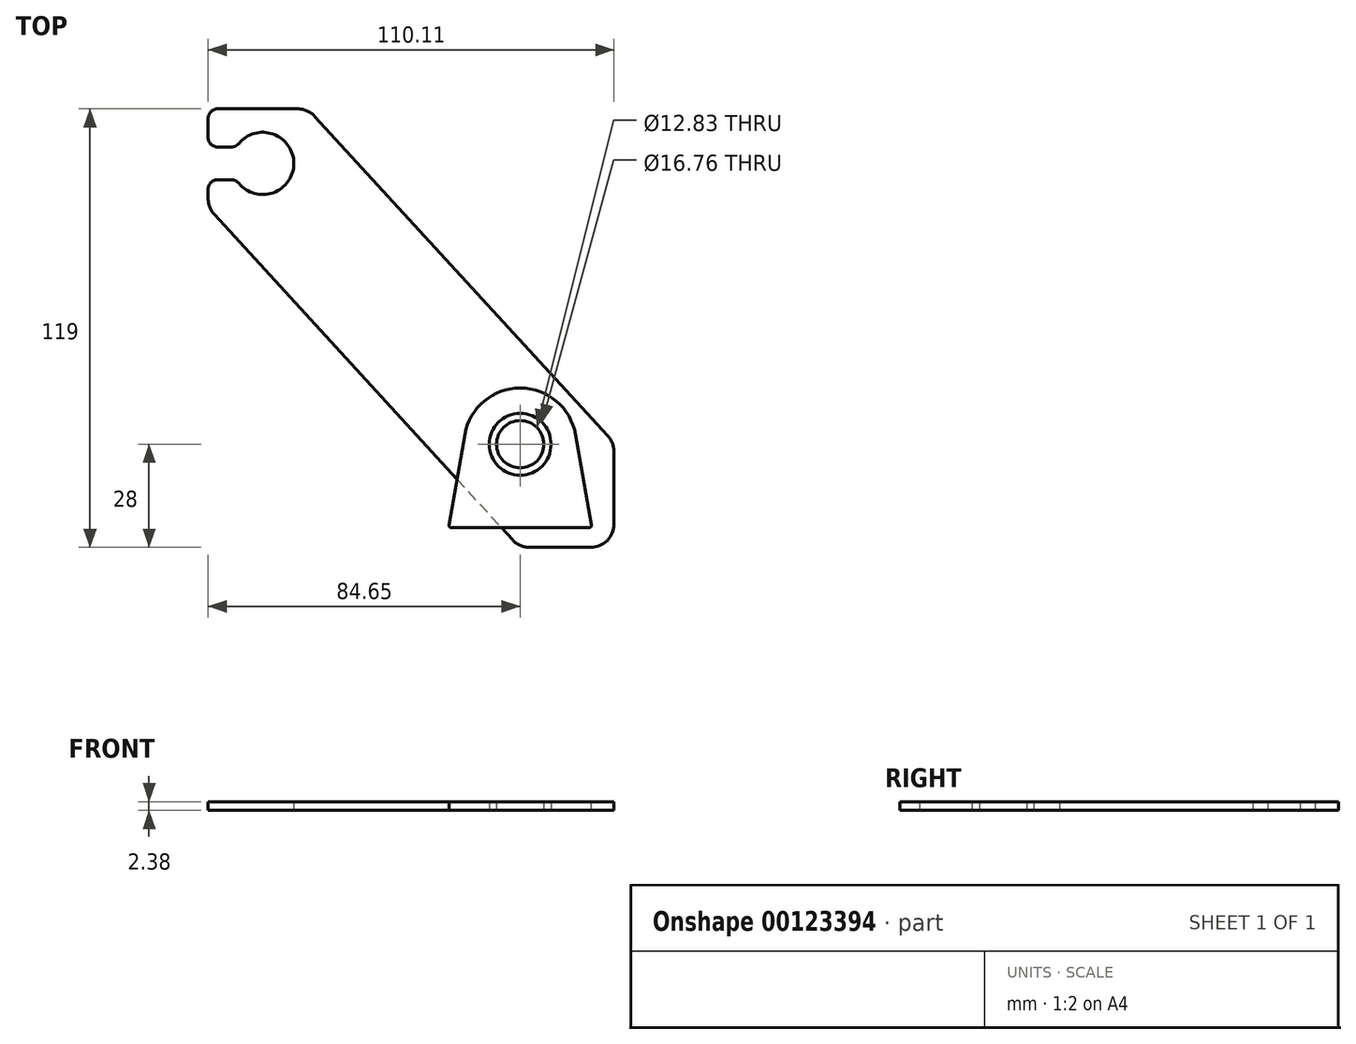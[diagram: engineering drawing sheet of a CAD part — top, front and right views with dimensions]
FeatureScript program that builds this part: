
annotation { "Feature Type Name" : "Feature", "Feature Type Description" : "" }
export const myFeature = defineFeature(function(context is Context, id is Id, definition is map)
    precondition{}
    {
        {
            var Q0;
            Q0=qCreatedBy(makeId("Top.planeOp"),FACE);
            var sketch = newSketch(context, id + "F0", { "sketchPlane" : qUnion([Q0])});
            skCircle(sketch, "E0", {"center": v(0, 0) * mm, "radius": 8.38 * mm});
            skCircle(sketch, "E1", {"center": v(0, 0) * mm, "radius": 8.26 * mm, "construction": true});
            skArc(sketch, "E2", {"start": v(-9.4, -7.26) * mm, "mid": v(0, -11.87) * mm, "end": v(9.4, -7.26) * mm, "construction": true});
            skLineSegment(sketch, "E3", {"start": v(-9.4, 7.26) * mm, "end": v(-9.4, -7.26) * mm, "construction": true});
            skLineSegment(sketch, "E4", {"start": v(0, 17.47) * mm, "end": v(0, -14.03) * mm, "construction": true});
            skLineSegment(sketch, "E5.MirrorCS", {"start": v(9.4, 7.26) * mm, "end": v(9.4, -7.26) * mm, "construction": true});
            skArc(sketch, "E6.trimOffspring", {"start": v(9.4, 7.26) * mm, "mid": v(0, 11.87) * mm, "end": v(-9.4, 7.26) * mm, "construction": true});
            skArc(sketch, "E7", {"start": v(15.24, 0) * mm, "mid": v(0, 15.24) * mm, "end": v(-15.24, 0) * mm});
            skArc(sketch, "E8", {"start": v(19.46, -22.61) * mm, "mid": v(0, -17.78) * mm, "end": v(-19.46, -22.61) * mm});
            skCircle(sketch, "E9", {"center": v(0, 0) * mm, "radius": 15.24 * mm});
            skLineSegment(sketch, "E10", {"start": v(-15, 2.65) * mm, "end": v(-19.46, -22.61) * mm});
            skLineSegment(sketch, "E11", {"start": v(-39.12, -20.64) * mm, "end": v(41.91, -20.64) * mm, "construction": true});
            skLineSegment(sketch, "E12.MirrorCS", {"start": v(15, 2.65) * mm, "end": v(19.46, -22.61) * mm});
            skLineSegment(sketch, "E13", {"start": v(-19.46, -22.61) * mm, "end": v(19.46, -22.61) * mm});
            skSolve(sketch);
        }
        {
            var Q0;
            Q0 = qSketchRegion(id + "F0", true);
            extrude(context, id + "F1", {"entities" : qUnion([Q0]), "depth" : 2.38 * mm});
        }
        {
            var Q0;
            Q0=makeQuery(id+"F1.opExtrude","SWEPT_EDGE",EDGE,{"disambiguationData":[OSD([sQuery(id+"F0.wireOp",EDGE,"E8"),sQuery(id+"F0.wireOp",EDGE,"E10")])]});
            var Q1;
            Q1=makeQuery(id+"F1.opExtrude","SWEPT_EDGE",EDGE,{"disambiguationData":[OSD([sQuery(id+"F0.wireOp",EDGE,"E8"),sQuery(id+"F0.wireOp",EDGE,"E12.MirrorCS")])]});
            fillet(context, id + "F2", {"entities" : qUnion([Q0, Q1]), "radius" : 0.64 * mm, "tangentPropagation" : true, "allowEdgeOverflow" : false});
        }
        {
            var Q0;
            Q0=qCreatedBy(makeId("Top.planeOp"),FACE);
            var sketch = newSketch(context, id + "F3", { "sketchPlane" : qUnion([Q0])});
            skCircle(sketch, "E14", {"center": v(0, 0) * mm, "radius": 6.41 * mm});
            skArc(sketch, "E15", {"start": v(-77.03, 71.75) * mm, "mid": v(-61.4, 76.2) * mm, "end": v(-77.03, 80.64) * mm});
            skLineSegment(sketch, "E16.bottom", {"start": v(-84.65, 91) * mm, "end": v(-57.57, 91) * mm});
            skLineSegment(sketch, "E16.top", {"start": v(-0.17, -28) * mm, "end": v(25.46, -28) * mm});
            skLineSegment(sketch, "E16.left", {"start": v(-84.65, 91) * mm, "end": v(-84.65, 80.64) * mm});
            skLineSegment(sketch, "E16.right", {"start": v(25.46, 0.41) * mm, "end": v(25.46, -28) * mm});
            skCircle(sketch, "E17", {"center": v(-69.85, 76.2) * mm, "radius": 14.8 * mm, "construction": true});
            skLineSegment(sketch, "E18", {"start": v(-6.41, 0) * mm, "end": v(-6.41, -28) * mm, "construction": true});
            skLineSegment(sketch, "E19", {"start": v(-84.65, 64.15) * mm, "end": v(-0.17, -28) * mm});
            skLineSegment(sketch, "E20", {"start": v(-57.57, 91) * mm, "end": v(25.46, 0.41) * mm});
            skLineSegment(sketch, "E21", {"start": v(0, 6.41) * mm, "end": v(25.46, 6.41) * mm, "construction": true});
            skLineSegment(sketch, "E22", {"start": v(-69.85, 76.2) * mm, "end": v(-84.65, 76.2) * mm, "construction": true});
            skLineSegment(sketch, "E23", {"start": v(-84.65, 80.64) * mm, "end": v(-77.03, 80.64) * mm});
            skLineSegment(sketch, "E24.MirrorCS", {"start": v(-84.65, 71.75) * mm, "end": v(-77.03, 71.75) * mm});
            skLineSegment(sketch, "E25.trimOffspring", {"start": v(-84.65, 71.75) * mm, "end": v(-84.65, 64.15) * mm});
            skLineSegment(sketch, "E26", {"start": v(-69.85, 76.2) * mm, "end": v(0, 0) * mm, "construction": true});
            skSolve(sketch);
        }
        {
            var Q0;
            Q0 = qSketchRegion(id + "F3", true);
            extrude(context, id + "F4", {"entities" : qUnion([Q0]), "depth" : 2.36 * mm});
        }
        {
            var Q0;
            Q0=makeQuery(id+"F4.opExtrude","SWEPT_EDGE",EDGE,{"disambiguationData":[OSD([sQuery(id+"F3.wireOp",EDGE,"bdc52bd2-ab92-457c-ac75-6660f9637d320.MirrorCS"),sQuery(id+"F3.wireOp",EDGE,"15c2a4e9-a582-4c82-bdb9-afa3fbdf7679.trimOffspring")])]});
            var Q1;
            Q1=makeQuery(id+"F4.opExtrude","SWEPT_EDGE",EDGE,{"disambiguationData":[OSD([sQuery(id+"F3.wireOp",EDGE,"94e997d7-6d58-4be6-b5bc-33bec046d831.0"),sQuery(id+"F3.wireOp",EDGE,"bdc52bd2-ab92-457c-ac75-6660f9637d320.MirrorCS")])]});
            var Q2;
            Q2=makeQuery(id+"F4.opExtrude","SWEPT_EDGE",EDGE,{"disambiguationData":[OSD([sQuery(id+"F3.wireOp",EDGE,"7wUlRdEc-HU2r-JPH0-r56L-MgtFaqzdT9Un.bottom"),sQuery(id+"F3.wireOp",EDGE,"r7xiSxnJ-VjEQ-WSqG-heHW-HxUJSaSldzg1")])]});
            var Q3;
            Q3=makeQuery(id+"F4.opExtrude","SWEPT_EDGE",EDGE,{"disambiguationData":[OSD([sQuery(id+"F3.wireOp",EDGE,"7wUlRdEc-HU2r-JPH0-r56L-MgtFaqzdT9Un.bottom"),sQuery(id+"F3.wireOp",EDGE,"7wUlRdEc-HU2r-JPH0-r56L-MgtFaqzdT9Un.left")])]});
            var Q4;
            Q4=makeQuery(id+"F4.opExtrude","SWEPT_EDGE",EDGE,{"disambiguationData":[OSD([sQuery(id+"F3.wireOp",EDGE,"7wUlRdEc-HU2r-JPH0-r56L-MgtFaqzdT9Un.right"),sQuery(id+"F3.wireOp",EDGE,"15c2a4e9-a582-4c82-bdb9-afa3fbdf7679.trimOffspring")])]});
            var Q5;
            Q5=makeQuery(id+"F4.opExtrude","SWEPT_EDGE",EDGE,{"disambiguationData":[OSD([sQuery(id+"F3.wireOp",EDGE,"94e997d7-6d58-4be6-b5bc-33bec046d831.0"),sQuery(id+"F3.wireOp",EDGE,"r7xiSxnJ-VjEQ-WSqG-heHW-HxUJSaSldzg1")])]});
            var Q6;
            Q6=makeQuery(id+"F4.opExtrude","SWEPT_EDGE",EDGE,{"disambiguationData":[OSD([sQuery(id+"F3.wireOp",EDGE,"7wUlRdEc-HU2r-JPH0-r56L-MgtFaqzdT9Un.top"),sQuery(id+"F3.wireOp",EDGE,"7wUlRdEc-HU2r-JPH0-r56L-MgtFaqzdT9Un.left")])]});
            var Q7;
            Q7=makeQuery(id+"F4.opExtrude","SWEPT_EDGE",EDGE,{"disambiguationData":[OSD([sQuery(id+"F3.wireOp",EDGE,"E16.bottom"),sQuery(id+"F3.wireOp",EDGE,"E20")])]});
            var Q8;
            Q8=makeQuery(id+"F4.opExtrude","SWEPT_EDGE",EDGE,{"disambiguationData":[OSD([sQuery(id+"F3.wireOp",EDGE,"E16.right"),sQuery(id+"F3.wireOp",EDGE,"E20")])]});
            var Q9;
            Q9=makeQuery(id+"F4.opExtrude","SWEPT_EDGE",EDGE,{"disambiguationData":[OSD([sQuery(id+"F3.wireOp",EDGE,"E16.top"),sQuery(id+"F3.wireOp",EDGE,"E16.right")])]});
            var Q10;
            Q10=makeQuery(id+"F4.opExtrude","SWEPT_EDGE",EDGE,{"disambiguationData":[OSD([sQuery(id+"F3.wireOp",EDGE,"E16.top"),sQuery(id+"F3.wireOp",EDGE,"E19")])]});
            var Q11;
            Q11=makeQuery(id+"F4.opExtrude","SWEPT_EDGE",EDGE,{"disambiguationData":[OSD([sQuery(id+"F3.wireOp",EDGE,"E19"),sQuery(id+"F3.wireOp",EDGE,"E25.trimOffspring")])]});
            fillet(context, id + "F5", {"entities" : qUnion([Q0, Q1, Q2, Q3, Q4, Q5, Q6, Q7, Q8, Q9, Q10, Q11]), "radius" : 6.35 * mm, "tangentPropagation" : true, "allowEdgeOverflow" : false});
        }
        {
            var Q0;
            Q0=makeQuery(id+"F4.opExtrude","SWEPT_EDGE",EDGE,{"disambiguationData":[OSD([sQuery(id+"F3.wireOp",EDGE,"E16.left"),sQuery(id+"F3.wireOp",EDGE,"E23")])]});
            var Q1;
            Q1=makeQuery(id+"F4.opExtrude","SWEPT_EDGE",EDGE,{"disambiguationData":[OSD([sQuery(id+"F3.wireOp",EDGE,"E24.MirrorCS"),sQuery(id+"F3.wireOp",EDGE,"E25.trimOffspring")])]});
            var Q2;
            Q2=makeQuery(id+"F4.opExtrude","SWEPT_EDGE",EDGE,{"disambiguationData":[OSD([sQuery(id+"F3.wireOp",EDGE,"E16.bottom"),sQuery(id+"F3.wireOp",EDGE,"E16.left")])]});
            var Q3;
            Q3=makeQuery(id+"F4.opExtrude","SWEPT_EDGE",EDGE,{"disambiguationData":[OSD([sQuery(id+"F3.wireOp",EDGE,"E15"),sQuery(id+"F3.wireOp",EDGE,"E23")])]});
            var Q4;
            Q4=makeQuery(id+"F4.opExtrude","SWEPT_EDGE",EDGE,{"disambiguationData":[OSD([sQuery(id+"F3.wireOp",EDGE,"E15"),sQuery(id+"F3.wireOp",EDGE,"E24.MirrorCS")])]});
            fillet(context, id + "F6", {"entities" : qUnion([Q0, Q1, Q2, Q3, Q4]), "radius" : 2.54 * mm, "tangentPropagation" : true, "allowEdgeOverflow" : false});
        }
    });
